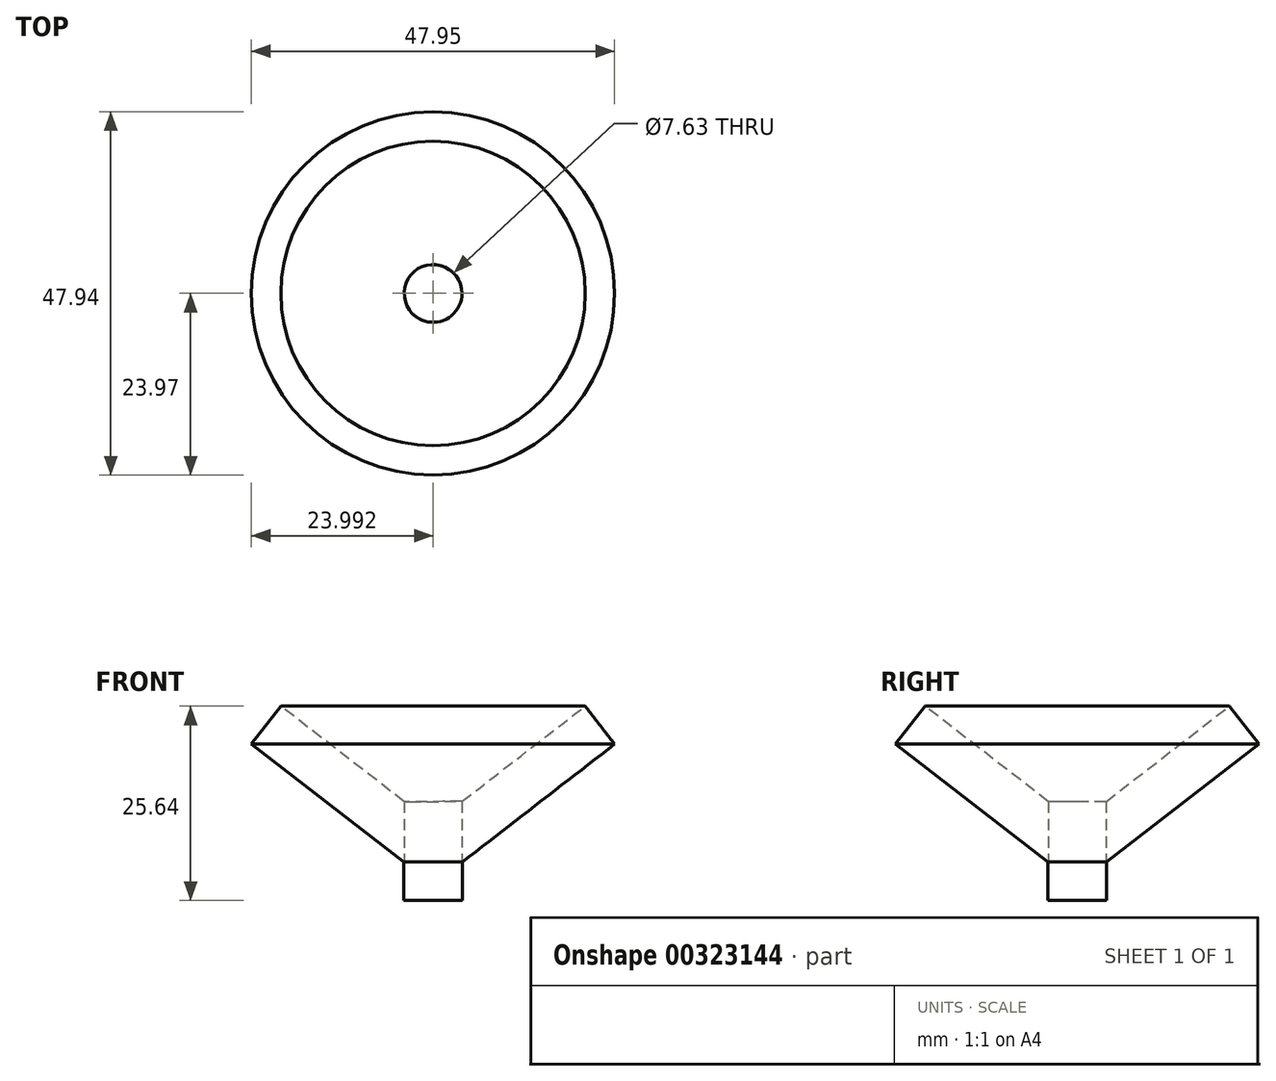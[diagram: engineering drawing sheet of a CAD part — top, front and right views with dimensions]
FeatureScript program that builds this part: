
annotation { "Feature Type Name" : "Feature", "Feature Type Description" : "" }
export const myFeature = defineFeature(function(context is Context, id is Id, definition is map)
    precondition{}
    {
        {
            var Q0;
            Q0=qCreatedBy(makeId("Front.planeOp"),FACE);
            var sketch = newSketch(context, id + "F0", { "sketchPlane" : qUnion([Q0])});
            skLineSegment(sketch, "E0", {"start": v(1.97, -2.72) * mm, "end": v(1.97, 2.36) * mm});
            skLineSegment(sketch, "E1", {"start": v(1.97, 2.36) * mm, "end": v(22.06, 17.9) * mm});
            skLineSegment(sketch, "E2", {"start": v(22.06, 17.9) * mm, "end": v(18.18, 22.92) * mm});
            skLineSegment(sketch, "E3", {"start": v(18.18, 22.92) * mm, "end": v(-1.91, 7.38) * mm});
            skLineSegment(sketch, "E4", {"start": v(-1.91, 7.38) * mm, "end": v(-1.91, -2.72) * mm});
            skLineSegment(sketch, "E5", {"start": v(-1.91, -2.72) * mm, "end": v(1.97, -2.72) * mm});
            skSolve(sketch);
        }
        {
            var Q0;
            Q0 = qSketchRegion(id + "F0", true);
            var Q1;
            Q1=sQuery(id+"F0.wireOp",EDGE,"E4");
            revolve(context, id + "F1", {"entities" : qUnion([Q0]), "axis" : qUnion([Q1]), "revolveType" : RevolveType.FULL});
        }
        {
            var Q0;
            Q0=qCreatedBy(makeId("Top.planeOp"),FACE);
            var sketch = newSketch(context, id + "F2", { "sketchPlane" : qUnion([Q0])});
            skCircle(sketch, "E6", {"center": v(-1.9, 0) * mm, "radius": 3.81 * mm});
            skSolve(sketch);
        }
        {
            var Q0;
            Q0 = qSketchRegion(id + "F2", true);
            extrude(context, id + "F3", {"entities" : qUnion([Q0]), "operationType" : NewBodyOperationType.REMOVE, "depth" : 38.1 * mm});
        }
        {
            var Q0;
            Q0=qCreatedBy(makeId("Top.planeOp"),FACE);
            var sketch = newSketch(context, id + "F4", { "sketchPlane" : qUnion([Q0])});
            skCircle(sketch, "E7", {"center": v(-1.9, 0) * mm, "radius": 3.02 * mm});
            skSolve(sketch);
        }
        {
            var Q0;
            Q0 = qSketchRegion(id + "F4", true);
            extrude(context, id + "F5", {"entities" : qUnion([Q0]), "operationType" : NewBodyOperationType.REMOVE, "depth" : 14.07 * mm});
        }
        {
            var Q0;
            Q0=makeQuery(id+"F3.boolean.opBoolean","COPY",FACE,{"derivedFrom":makeQuery(id+"F3.opExtrude","CAP_FACE",FACE,{"disambiguationData":[OSD([sQuery(id+"F2.wireOp",EDGE,"E6")])],"isStart":true})});
            extrude(context, id + "F6", {"entities" : qUnion([Q0]), "operationType" : NewBodyOperationType.REMOVE, "oppositeDirection" : true, "depth" : 15.24 * mm});
        }
    });
